# Revit family: Sanitary-Equipment_Duravit_Urinal-Ben_084737
name_source: partatom
category: Plumbing Fixtures
revit_build: Autodesk Revit 2014 (Build: 20130308_1515(x64)
units: mm (PartAtom-declared; Revit-internal decimal feet)

## types (1)
- 084737 White Alpin
    BIMobject category = Urinals
    Depth (mm) = 350 mm  [stored 1.14829 ft]
    Description = Urinal concealed inlet, syphonic action, vertical or horizontal outlet.
    Drain Diameter (mm) = 50 mm  [stored 0.164042 ft]
    Edition number = 1
    Height (mm) = 705 mm  [stored 2.31299 ft]
    IFC Classification = Sanitary Terminal
    Installation instructions = http://pro.duravit.com
    Manufacturer = Duravit
    Manufacturer name = DURAVIT
    Masterformat 2014 Code = 22 41 13.16
    Masterformat 2014 Description = Residential Urinals
    Model = 084737
    Mounting Height (mm) = 1075 mm
    NBS Reference Code = 31-93
    NBS Reference Description = Urinal And Wc Fittings
    Nominal height = 0 mm  [stored 0 ft]
    Nominal width = 350 mm  [stored 1.14829 ft]
    OmniClass Code = 23-31 21 00
    OmniClass Description = Urinals
    Option 01 = Options : Model without fly
    Option 02 = Options : Model with fly
    Primary Material = Ceramics-Duravit-White_Alpin
    Product Guid = 04bac0ad-92fe-44b5-b44d-9291ac7fafd9
    Product SKU = urinals-urinal-ben-084737
    Product certification = http://pro.duravit.com
    Product data url = https://bimobject.com
    Product family = Urinals
    Product group = Urinal Ben
    QR code = http://bimobject.com
    Specification = 0847370000: Urinal Ben white concealed inlet 0847370007: Urinal Ben white concealed inlet, with fly 08473700071: Urinal Ben white concealed inlet, with fly, WG
    Technical description = http://pro.duravit.com
    UNSPSC Code = 30181506
    URL = http://www.duravit.de
    Uniclass 1.4 Code = L721
    Uniclass 1.4 Description = Sanitary equipment
    Uniclass 2.0 Code = PR-31-93
    Uniclass 2.0 Description = Urinal And Wc Fittings
    Uniclass 2015 Code = Pr_40_20_93
    Uniclass 2015 Name = Urinal and WC fittings
    Uniformat II Code = D2010
    Uniformat II Description = Plumbing Fixtures
    Water Inlet Diameter (mm) = 35 mm  [stored 0.114829 ft]
    Weight Net (Kg) = 16.5
    Width (mm) = 370 mm  [stored 1.21391 ft]

note: [stored X ft] marks values corroborated as IEEE doubles in the binary element streams (Revit-internal decimal feet)

## geometry (parser evidence)
native form markers: Sweep x6
no freeform markers — native parametric forms only
